# Revit family: HBB 510 B
name_source: partatom
category: Specialty Equipment
revit_build: Autodesk Revit 2017 (Build: 20160225_1515(x64)
units: mm (PartAtom-declared; Revit-internal decimal feet)

## family parameters
Always vertical = Yes
Cut with Voids When Loaded = No
Part Type = Normal
Room Calculation Point = No
Round Connector Dimension = Use Diameter
Shared = No
Work Plane-Based = No

## types (1)
- HBB 510 Blanco
    Acabado Horno = Teka_Acero Inox
    Borde Aluminio = Teka_Panel Blanco
    Ca_1_Cable de conexión = 100 mm  [stored 0.328084 ft]
    Ca_1_Potencia nominal max. W. = 2593
    Ca_2_Iluminación Interior = 1 x 25W
    Ca_2_Motor Refrigeración = 18 W
    Ca_2_Resistencia Grill: Normal/Maxi-Grill = 1400/-
    Ca_2_Resistencia Inferior = 1150 W
    Ca_2_Resistencia Turbo = 0 W
    Ca_2_Resistencia superior + inferior = 2550 W
    Ca_3_Display Digital = No
    Ca_3_Guías laterales cromadas = Yes
    Ca_3_Mandos Pop Up = No
    Ca_3_N° de Funciones de cocinado = 3
    Ca_3_Programador - Temporizador de Paro = Yes
    Ca_3_Salida de vahos integrada = Bóveda
    Ca_3_Sistema de guías extraibles = -
    Ca_3_Ventilación Tangencial con optimización de salida = Yes
    Ca_4_Anti-vuelco de parrillas = Yes
    Ca_4_Bloqueo de seguridad del panel = No
    Ca_4_Cristal Puerta = 2
    Ca_4_Desconexión automática en puerta = No
    Ca_4_Protector del grill = Yes
    Ca_4_Termostato de seguridad = Yes
    Ca_5_Acero Inox Anti-huella = No
    Ca_5_Esmalte Crystal Clean = No
    Ca_5_Esmalte Hydroclean™ = Yes
    Ca_6_Asa para extracción de bandejas = No
    Ca_6_Asador rotativo = No
    Ca_6_Bandeja Pastelera = No
    Ca_6_Bandeja de asados profunda 50mm = 1
    Ca_6_Bandeja modular con tapa de cristal = No
    Ca_6_Parrilla reforzada de asados-cromada = 1
    Ca_Alto = 595 mm
    Ca_Ancho = 595 mm
    Ca_Capacidad en Litros = 76
    Ca_Certificaciones = Certificación SEC
    Ca_Clase de Eficiencia Energética = A
    Ca_Creado por = Catálogo Arquitectura
    Ca_Código Catálogo Arquitectura = 465_TEK_012
    Ca_Código EAN = 8421152148921
    Ca_Código del Producto = 41560031
    Ca_Especificaciones Técnicas = Horno eléctrico multifunción empotrable para muebles de cocina modelo HBB 510 WH
    Ca_Fabricante = Teka
    Ca_Instalación = Empotrado
    Ca_Itemizado CDT = E 08 06 02
    Ca_Masterformat = 11 30 13.13
    Ca_Material Principal = Acero Esmaltado+Cristal Templado
    Ca_Medidas de embalaje = 650 x 635 x 655 mm
    Ca_País de Fabricación = España
    Ca_Peso = 28 kg
    Ca_Producto = Horno HBB 510 WH
    Ca_Profundidad = 559 mm  [stored 1.83399 ft]
    Ca_Representante = Teka
    Ca_Teléfono = 99821 1017
    Ca_Usos = Horno eléctrico estático empotrable para muebles de cocina
    Ca_Web del Fabricante = www.teka.com
    Ca_Web del Representante = www.teka.cl
    Description = Horno eléctrico estático empotrable para muebles de cocina
    Interior Negro = Teka_Interior Negro
    Letras = Teka_Logo Negro
    Letras Negras = Teka_Panel Negro
    Logo Teka = Teka_Logo Blanco
    Manufacturer = Teka
    Model = HBB 510 WH
    Panel Menu = Teka_Panel Interior
    Panel Vidrio = Teka_Panel Vidrio Blanco
    Paneles = Teka_Panel Blanco
    Perilla Aluminio = Teka_Acero Inox
    Perilla Negro = Teka_Perilla Negro
    URL = www.teka.cl

note: [stored X ft] marks values corroborated as IEEE doubles in the binary element streams (Revit-internal decimal feet)
